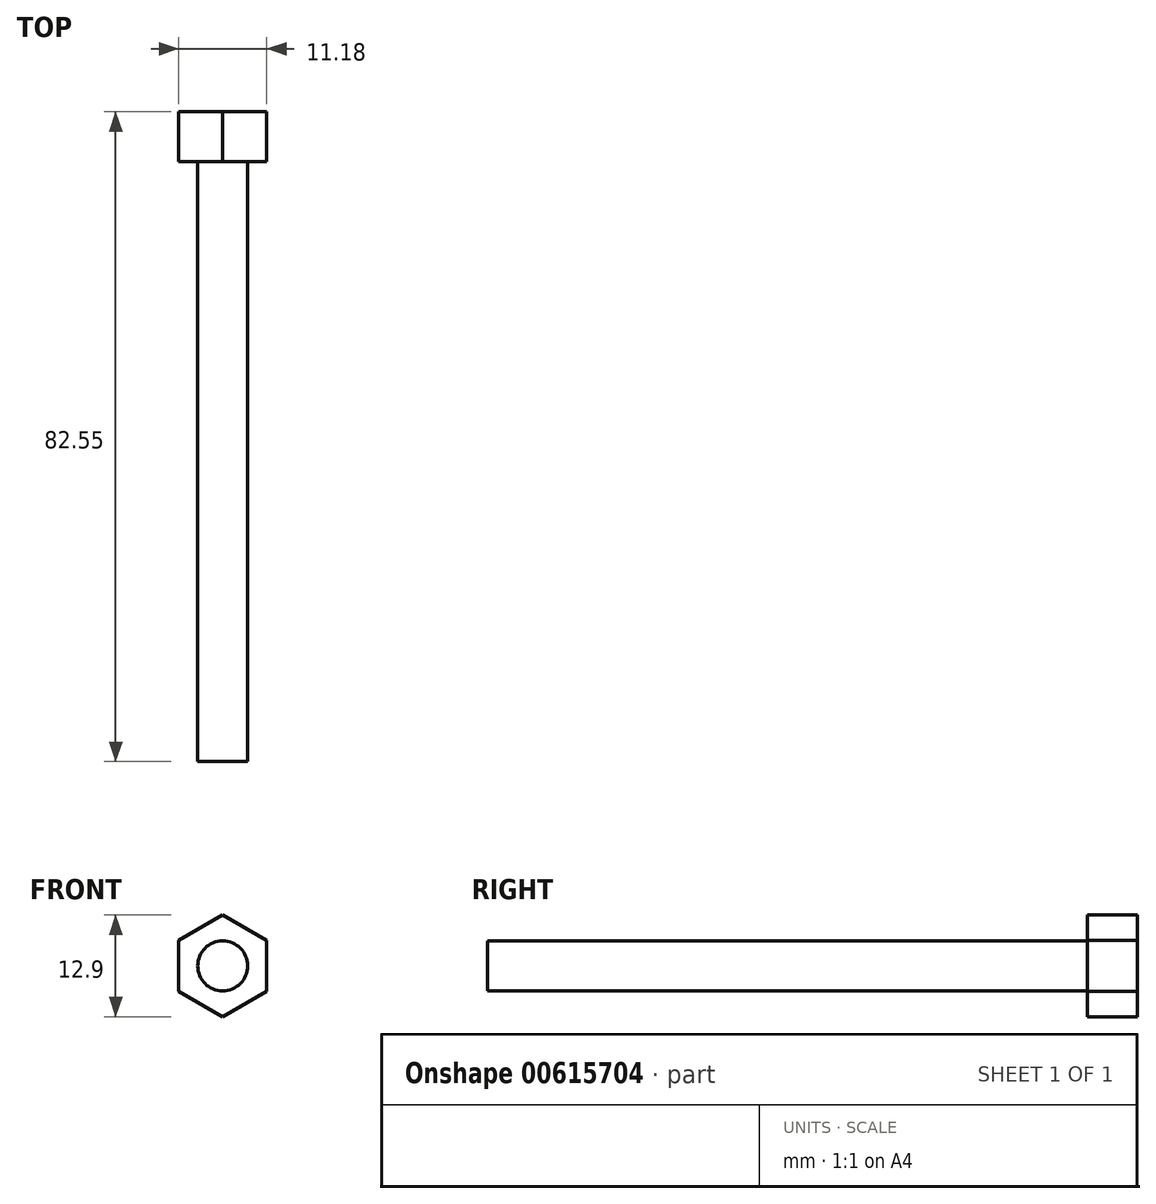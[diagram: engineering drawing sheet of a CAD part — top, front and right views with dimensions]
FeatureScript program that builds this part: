
annotation { "Feature Type Name" : "Feature", "Feature Type Description" : "" }
export const myFeature = defineFeature(function(context is Context, id is Id, definition is map)
    precondition{}
    {
        {
            var Q0;
            Q0=qCreatedBy(makeId("Front.planeOp"),FACE);
            var sketch = newSketch(context, id + "F0", { "sketchPlane" : qUnion([Q0])});
            skCircle(sketch, "E0", {"center": v(0, 0) * mm, "radius": 3.17 * mm});
            skSolve(sketch);
        }
        {
            var Q0;
            Q0 = qSketchRegion(id + "F0", true);
            extrude(context, id + "F1", {"entities" : qUnion([Q0]), "depth" : 76.2 * mm, "offsetDistance" : 25.4 * mm});
        }
        {
            var Q0;
            Q0=makeQuery(id+"F1.opExtrude","CAP_FACE",FACE,{"disambiguationData":[OSD([sQuery(id+"F0.wireOp",EDGE,"E0")])],"isStart":true});
            var sketch = newSketch(context, id + "F2", { "sketchPlane" : qUnion([Q0])});
            skCircle(sketch, "E1.cCircle", {"center": v(0, 0) * mm, "radius": 5.59 * mm, "construction": true});
            skLineSegment(sketch, "E1.0", {"start": v(5.59, 3.23) * mm, "end": v(5.59, -3.23) * mm});
            skLineSegment(sketch, "E1.1", {"start": v(5.59, -3.23) * mm, "end": v(0, -6.45) * mm});
            skLineSegment(sketch, "E1.2", {"start": v(0, -6.45) * mm, "end": v(-5.59, -3.23) * mm});
            skLineSegment(sketch, "E1.3", {"start": v(-5.59, -3.23) * mm, "end": v(-5.59, 3.23) * mm});
            skLineSegment(sketch, "E1.4", {"start": v(-5.59, 3.23) * mm, "end": v(0, 6.45) * mm});
            skLineSegment(sketch, "E1.5", {"start": v(0, 6.45) * mm, "end": v(5.59, 3.23) * mm});
            skPoint(sketch, "E1.0.midPoint", {"position": v(5.59, 0) * mm});
            skSolve(sketch);
        }
        {
            var Q0;
            Q0=makeQuery(id+"F2.imprint","IMPRINT",FACE,{"disambiguationData":[TD([[makeQuery(id+"F2.imprint","IMPRINT",EDGE,{"derivedFrom":sQuery(id+"F2.wireOp",EDGE,"E1.0")}),-1.0]])]});
            var Q1;
            Q1=makeQuery(id+"F2.imprint","IMPRINT",FACE,{"disambiguationData":[TD([[makeQuery(id+"F2.imprint","IMPRINT",EDGE,{"derivedFrom":makeQuery(id+"F1.opExtrude","CAP_EDGE",EDGE,{"disambiguationData":[OSD([sQuery(id+"F0.wireOp",EDGE,"E0")])],"isStart":true})}),-1.0]])]});
            extrude(context, id + "F3", {"entities" : qUnion([Q0, Q1]), "operationType" : NewBodyOperationType.ADD, "depth" : 6.35 * mm, "offsetDistance" : 25.4 * mm});
        }
    });
